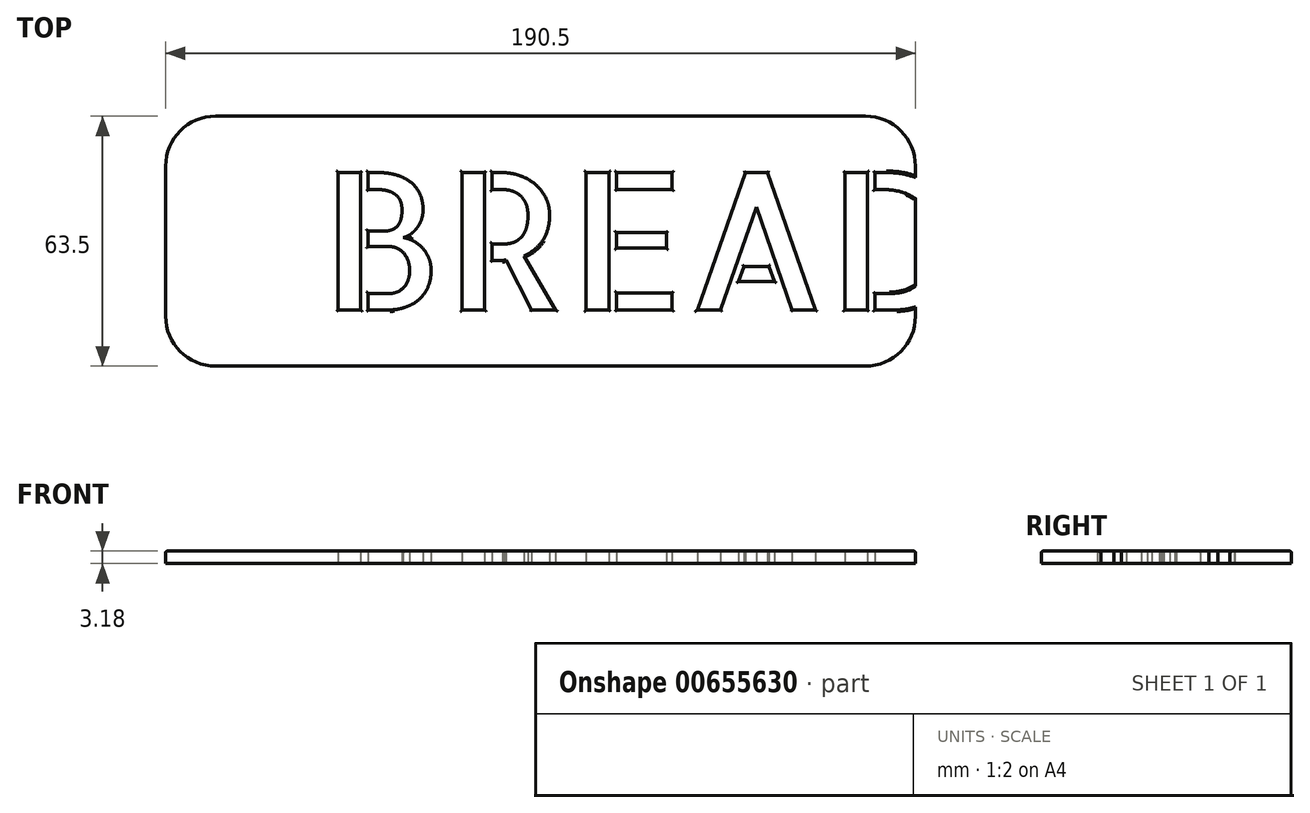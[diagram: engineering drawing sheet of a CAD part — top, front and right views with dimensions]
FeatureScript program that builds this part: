
annotation { "Feature Type Name" : "Feature", "Feature Type Description" : "" }
export const myFeature = defineFeature(function(context is Context, id is Id, definition is map)
    precondition{}
    {
        {
            var Q0;
            Q0=qCreatedBy(makeId("Top.planeOp"),FACE);
            var sketch = newSketch(context, id + "F0", { "sketchPlane" : qUnion([Q0])});
            skLineSegment(sketch, "E0.bottom", {"start": v(12.7, 0) * mm, "end": v(177.8, 0) * mm});
            skLineSegment(sketch, "E0.top", {"start": v(12.7, 63.5) * mm, "end": v(177.8, 63.5) * mm});
            skLineSegment(sketch, "E0.left", {"start": v(0, 12.7) * mm, "end": v(0, 50.8) * mm});
            skLineSegment(sketch, "E0.right", {"start": v(190.5, 12.7) * mm, "end": v(190.5, 50.8) * mm});
            skPoint(sketch, "E1.visualSharp", {"position": v(0, 63.5) * mm});
            skArc(sketch, "E1.filletArc", {"start": v(12.7, 63.5) * mm, "mid": v(3.72, 59.78) * mm, "end": v(0, 50.8) * mm});
            skPoint(sketch, "E2.visualSharp", {"position": v(0, 0) * mm});
            skArc(sketch, "E2.filletArc", {"start": v(0, 12.7) * mm, "mid": v(3.72, 3.72) * mm, "end": v(12.7, 0) * mm});
            skPoint(sketch, "E3.visualSharp", {"position": v(190.5, 0) * mm});
            skArc(sketch, "E3.filletArc", {"start": v(177.8, 0) * mm, "mid": v(186.78, 3.72) * mm, "end": v(190.5, 12.7) * mm});
            skPoint(sketch, "E4.visualSharp", {"position": v(190.5, 63.5) * mm});
            skArc(sketch, "E4.filletArc", {"start": v(190.5, 50.8) * mm, "mid": v(186.78, 59.78) * mm, "end": v(177.8, 63.5) * mm});
            skSolve(sketch);
        }
        {
            var Q0;
            Q0=qSketchRegion(id+"F0",true);
            extrude(context, id + "F1", {"entities" : qUnion([Q0]), "depth" : 3.17 * mm, "offsetDistance" : 25.4 * mm});
        }
        {
            var Q0;
            Q0=qCreatedBy(makeId("Top.planeOp"),FACE);
            var sketch = newSketch(context, id + "F2", { "sketchPlane" : qUnion([Q0])});
            skText(sketch, "E5", { "text": "BREAD", "fontName": "AllertaStencil-Regular.ttf"});
            const initialGuessF2  = {"E5": [0.0393, 0.01429, 1, 0, 0.03492]};
            skSetInitialGuess(sketch, initialGuessF2);
            skSolve(sketch);
        }
        {
            var Q0;
            Q0=qSketchRegion(id+"F2",true);
            extrude(context, id + "F3", {"entities" : qUnion([Q0]), "operationType" : NewBodyOperationType.REMOVE, "endBound" : BoundingType.THROUGH_ALL, "depth" : 25.4 * mm, "offsetDistance" : 25.4 * mm});
        }
        {
            var Q0;
            Q0=makeQuery(id+"F1.opExtrude","CAP_FACE",FACE,{"disambiguationData":[OSD([sQuery(id+"F0.wireOp",EDGE,"E0.bottom"),sQuery(id+"F0.wireOp",EDGE,"E0.top"),sQuery(id+"F0.wireOp",EDGE,"E0.left"),sQuery(id+"F0.wireOp",EDGE,"E0.right"),sQuery(id+"F0.wireOp",EDGE,"E1.filletArc"),sQuery(id+"F0.wireOp",EDGE,"E2.filletArc"),sQuery(id+"F0.wireOp",EDGE,"E3.filletArc"),sQuery(id+"F0.wireOp",EDGE,"E4.filletArc")])],"isStart":false});
            fillet(context, id + "F4", {"entities" : qUnion([Q0]), "radius" : 0.38 * mm, "tangentPropagation" : true, "allowEdgeOverflow" : false});
        }
    });
